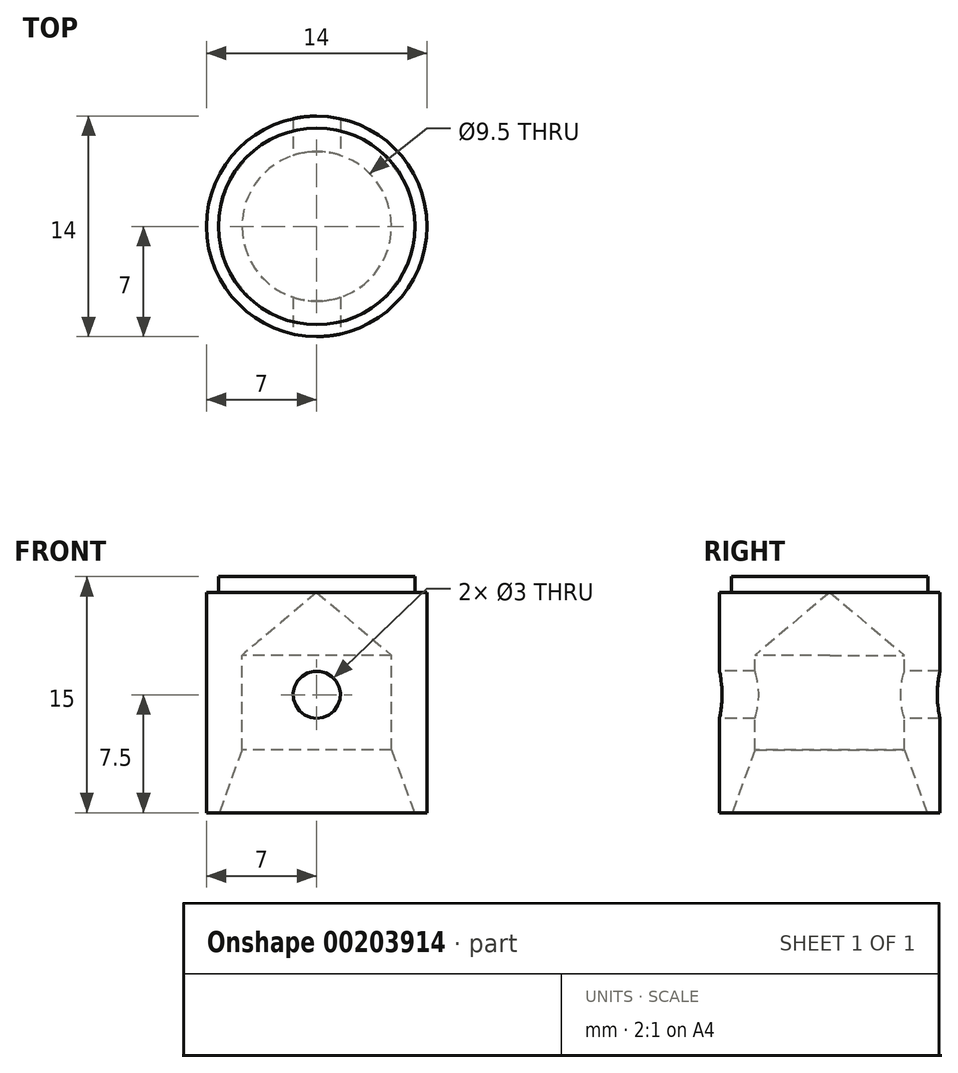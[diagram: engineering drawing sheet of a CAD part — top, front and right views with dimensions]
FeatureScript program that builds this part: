
annotation { "Feature Type Name" : "Feature", "Feature Type Description" : "" }
export const myFeature = defineFeature(function(context is Context, id is Id, definition is map)
    precondition{}
    {
        {
            var Q0;
            Q0=qCreatedBy(makeId("Front.planeOp"),FACE);
            var sketch = newSketch(context, id + "F0", { "sketchPlane" : qUnion([Q0])});
            skLineSegment(sketch, "E0", {"start": v(0, 43.09) * mm, "end": v(0, -41.63) * mm, "construction": true});
            skLineSegment(sketch, "E1", {"start": v(-36.72, 0) * mm, "end": v(43.28, 0) * mm, "construction": true});
            skLineSegment(sketch, "E2.bottom", {"start": v(7, 7.5) * mm, "end": v(-7, 7.5) * mm, "construction": true});
            skLineSegment(sketch, "E2.top", {"start": v(7, -7.5) * mm, "end": v(-7, -7.5) * mm, "construction": true});
            skLineSegment(sketch, "E2.left", {"start": v(7, 7.5) * mm, "end": v(7, -7.5) * mm, "construction": true});
            skLineSegment(sketch, "E2.right", {"start": v(-7, 7.5) * mm, "end": v(-7, -7.5) * mm, "construction": true});
            skPoint(sketch, "E2.middle", {"position": v(0, 0) * mm});
            skLineSegment(sketch, "E3", {"start": v(-7, -7.5) * mm, "end": v(-7, 6.5) * mm});
            skLineSegment(sketch, "E4", {"start": v(-7, 6.5) * mm, "end": v(-6.25, 6.5) * mm});
            skLineSegment(sketch, "E5", {"start": v(-6.25, 6.5) * mm, "end": v(-6.25, 7.5) * mm});
            skLineSegment(sketch, "E6", {"start": v(-6.25, 7.5) * mm, "end": v(0, 7.5) * mm});
            skLineSegment(sketch, "E7", {"start": v(0, 7.5) * mm, "end": v(0, 6.5) * mm});
            skLineSegment(sketch, "E8", {"start": v(0, 6.5) * mm, "end": v(0, 2.5) * mm, "construction": true});
            skLineSegment(sketch, "E9", {"start": v(0, 2.5) * mm, "end": v(-4.75, 2.5) * mm, "construction": true});
            skLineSegment(sketch, "E10", {"start": v(0, 6.5) * mm, "end": v(-4.75, 2.5) * mm});
            skLineSegment(sketch, "E11", {"start": v(-4.75, 2.5) * mm, "end": v(-4.75, -7.5) * mm, "construction": true});
            skLineSegment(sketch, "E12", {"start": v(-4.75, -7.5) * mm, "end": v(-6.2, -7.5) * mm, "construction": true});
            skLineSegment(sketch, "E13", {"start": v(-6.2, -7.5) * mm, "end": v(-4.75, -3.52) * mm});
            skLineSegment(sketch, "E14", {"start": v(-4.75, 2.5) * mm, "end": v(-4.75, -3.52) * mm});
            skLineSegment(sketch, "E15", {"start": v(-6.2, -7.5) * mm, "end": v(-7, -7.5) * mm});
            skCircle(sketch, "E16", {"center": v(0, 0) * mm, "radius": 1.5 * mm});
            skSolve(sketch);
        }
        {
            var Q0;
            Q0=makeQuery(id+"F0.imprint","IMPRINT",FACE,{"disambiguationData":[TD([[makeQuery(id+"F0.imprint","IMPRINT",EDGE,{"derivedFrom":sQuery(id+"F0.wireOp",EDGE,"E3")}),-1.0]])]});
            var Q1;
            Q1=sQuery(id+"F0.wireOp",EDGE,"E0");
            revolve(context, id + "F1", {"entities" : qUnion([Q0]), "axis" : qUnion([Q1]), "revolveType" : RevolveType.FULL});
        }
        {
            var Q0;
            Q0=qCreatedBy(makeId("Front.planeOp"),FACE);
            cPlane(context, id + "F2", {"entities" : qUnion([Q0]), "cplaneType" : CPlaneType.OFFSET, "offset" : 7 * mm, "width" : 150 * mm, "height" : 150 * mm});
        }
        {
            var Q0;
            Q0=qCreatedBy(id+"F2.planeOp",FACE);
            var sketch = newSketch(context, id + "F3", { "sketchPlane" : qUnion([Q0])});
            skCircle(sketch, "E17.0", {"center": v(0, 0) * mm, "radius": 1.5 * mm});
            skSolve(sketch);
        }
        {
            var Q0;
            Q0=qSketchRegion(id+"F3",true);
            extrude(context, id + "F4", {"entities" : qUnion([Q0]), "operationType" : NewBodyOperationType.REMOVE, "endBound" : BoundingType.THROUGH_ALL, "oppositeDirection" : true, "depth" : 25 * mm});
        }
    });
